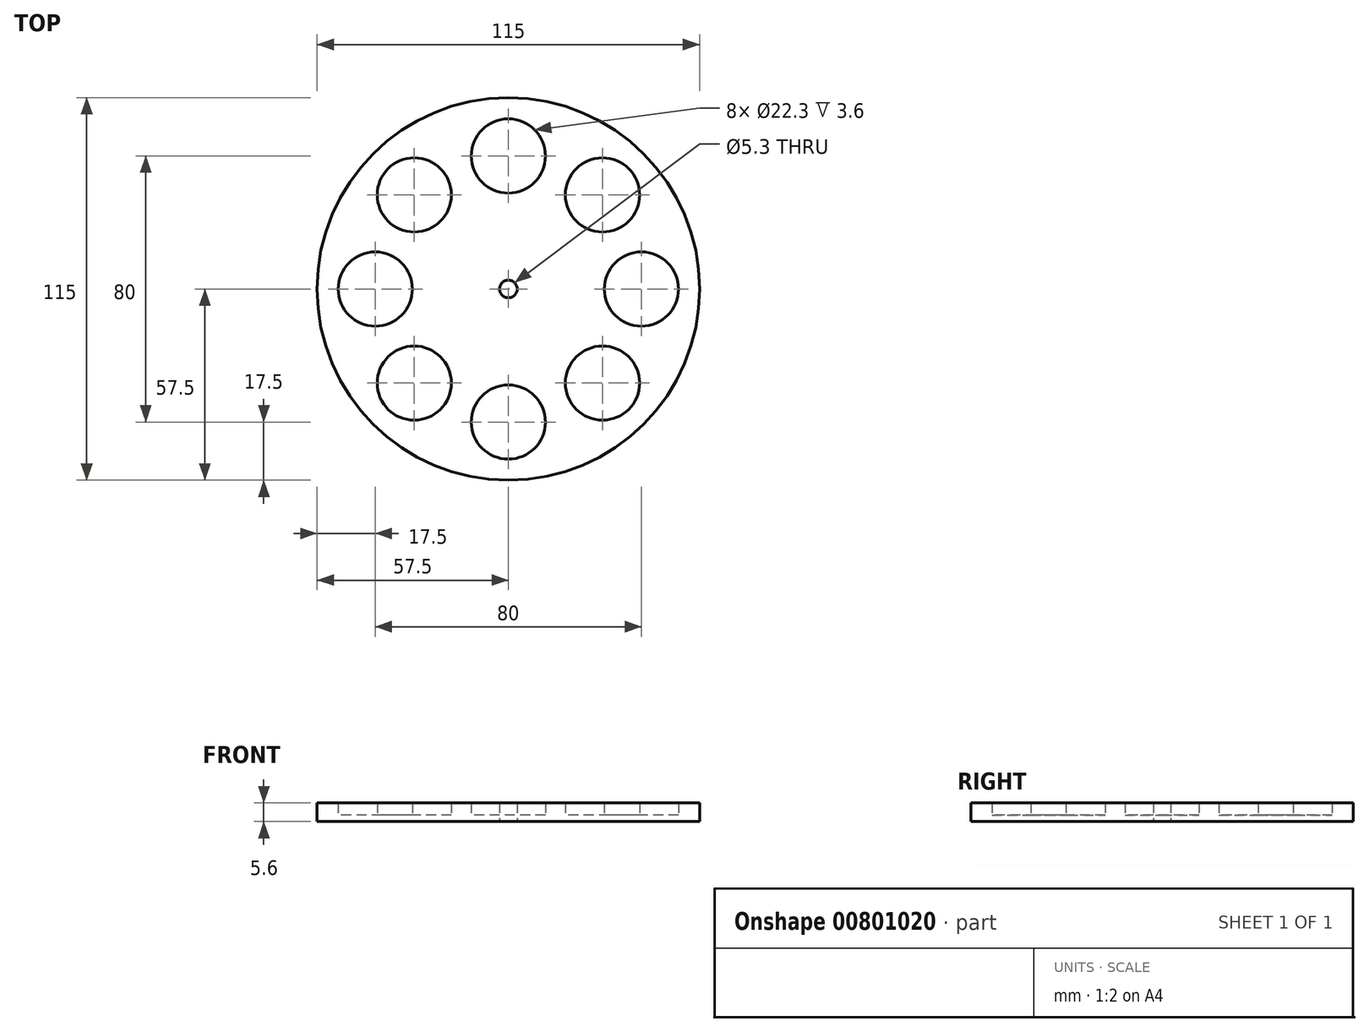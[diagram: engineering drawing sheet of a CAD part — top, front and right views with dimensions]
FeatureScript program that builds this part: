
annotation { "Feature Type Name" : "Feature", "Feature Type Description" : "" }
export const myFeature = defineFeature(function(context is Context, id is Id, definition is map)
    precondition{}
    {
        {
            var Q0;
            Q0=qCreatedBy(makeId("Top.planeOp"),FACE);
            var sketch = newSketch(context, id + "F0", { "sketchPlane" : qUnion([Q0])});
            skCircle(sketch, "E0", {"center": v(0, 0) * mm, "radius": 57.5 * mm});
            skCircle(sketch, "E1", {"center": v(0, 0) * mm, "radius": 2.65 * mm});
            skCircle(sketch, "E2", {"center": v(-40, 0) * mm, "radius": 11.15 * mm});
            skCircle(sketch, "E3.1.0", {"center": v(-28.28, -28.28) * mm, "radius": 11.15 * mm});
            skCircle(sketch, "E3.2.0", {"center": v(0, -40) * mm, "radius": 11.15 * mm});
            skCircle(sketch, "E3.3.0", {"center": v(28.28, -28.28) * mm, "radius": 11.15 * mm});
            skCircle(sketch, "E3.4.0", {"center": v(40, 0) * mm, "radius": 11.15 * mm});
            skCircle(sketch, "E3.5.0", {"center": v(28.28, 28.28) * mm, "radius": 11.15 * mm});
            skCircle(sketch, "E3.6.0", {"center": v(0, 40) * mm, "radius": 11.15 * mm});
            skCircle(sketch, "E3.7.0", {"center": v(-28.28, 28.28) * mm, "radius": 11.15 * mm});
            skSolve(sketch);
        }
        {
            var Q0;
            Q0=makeQuery(id+"F0.imprint","IMPRINT",FACE,{"disambiguationData":[TD([[makeQuery(id+"F0.imprint","IMPRINT",EDGE,{"derivedFrom":sQuery(id+"F0.wireOp",EDGE,"E0")}),1.0]])]});
            extrude(context, id + "F1", {"entities" : qUnion([Q0]), "depth" : 3.6 * mm, "offsetDistance" : 25.4 * mm});
        }
        {
            var Q0;
            Q0=makeQuery(id+"F0.imprint","IMPRINT",FACE,{"disambiguationData":[TD([[makeQuery(id+"F0.imprint","IMPRINT",EDGE,{"derivedFrom":sQuery(id+"F0.wireOp",EDGE,"E3.1.0")}),1.0]])]});
            var Q1;
            Q1=makeQuery(id+"F0.imprint","IMPRINT",FACE,{"disambiguationData":[TD([[makeQuery(id+"F0.imprint","IMPRINT",EDGE,{"derivedFrom":sQuery(id+"F0.wireOp",EDGE,"E3.2.0")}),1.0]])]});
            var Q2;
            Q2=makeQuery(id+"F0.imprint","IMPRINT",FACE,{"disambiguationData":[TD([[makeQuery(id+"F0.imprint","IMPRINT",EDGE,{"derivedFrom":sQuery(id+"F0.wireOp",EDGE,"E3.3.0")}),1.0]])]});
            var Q3;
            Q3=makeQuery(id+"F0.imprint","IMPRINT",FACE,{"disambiguationData":[TD([[makeQuery(id+"F0.imprint","IMPRINT",EDGE,{"derivedFrom":sQuery(id+"F0.wireOp",EDGE,"E3.4.0")}),1.0]])]});
            var Q4;
            Q4=makeQuery(id+"F0.imprint","IMPRINT",FACE,{"disambiguationData":[TD([[makeQuery(id+"F0.imprint","IMPRINT",EDGE,{"derivedFrom":sQuery(id+"F0.wireOp",EDGE,"E3.5.0")}),1.0]])]});
            var Q5;
            Q5=makeQuery(id+"F0.imprint","IMPRINT",FACE,{"disambiguationData":[TD([[makeQuery(id+"F0.imprint","IMPRINT",EDGE,{"derivedFrom":sQuery(id+"F0.wireOp",EDGE,"E3.6.0")}),1.0]])]});
            var Q6;
            Q6=makeQuery(id+"F0.imprint","IMPRINT",FACE,{"disambiguationData":[TD([[makeQuery(id+"F0.imprint","IMPRINT",EDGE,{"derivedFrom":sQuery(id+"F0.wireOp",EDGE,"E3.7.0")}),1.0]])]});
            var Q7;
            Q7=makeQuery(id+"F0.imprint","IMPRINT",FACE,{"disambiguationData":[TD([[makeQuery(id+"F0.imprint","IMPRINT",EDGE,{"derivedFrom":sQuery(id+"F0.wireOp",EDGE,"E2")}),1.0]])]});
            var Q8;
            Q8=makeQuery(id+"F0.imprint","IMPRINT",FACE,{"disambiguationData":[TD([[makeQuery(id+"F0.imprint","IMPRINT",EDGE,{"derivedFrom":sQuery(id+"F0.wireOp",EDGE,"E0")}),1.0]])]});
            extrude(context, id + "F2", {"entities" : qUnion([Q0, Q1, Q2, Q3, Q4, Q5, Q6, Q7, Q8]), "operationType" : NewBodyOperationType.ADD, "oppositeDirection" : true, "depth" : 2 * mm, "offsetDistance" : 25.4 * mm});
        }
    });
